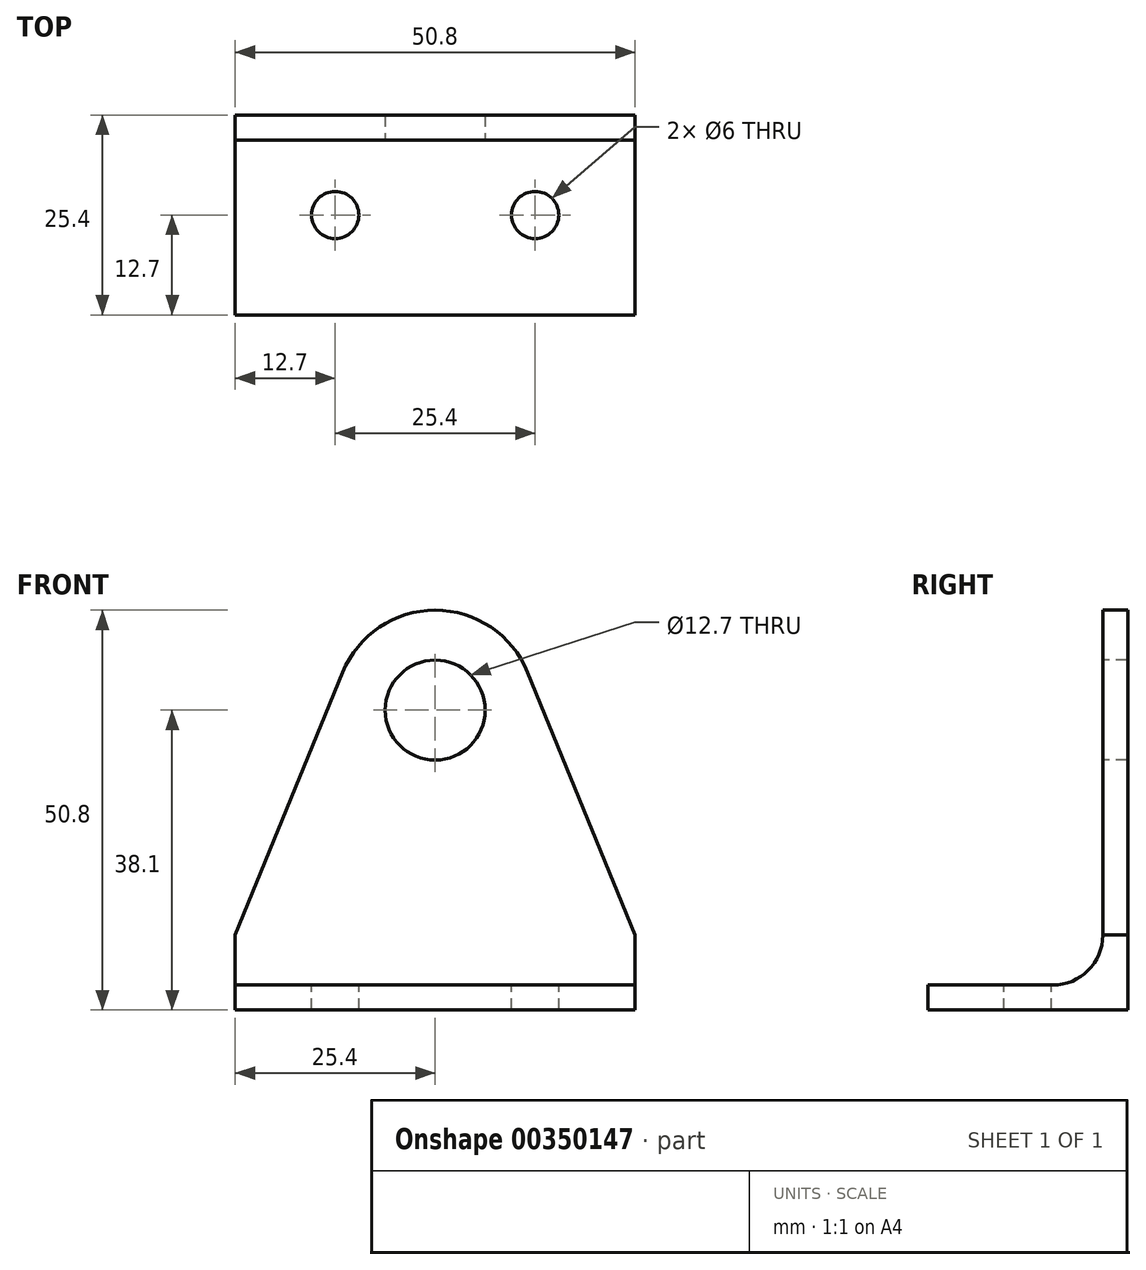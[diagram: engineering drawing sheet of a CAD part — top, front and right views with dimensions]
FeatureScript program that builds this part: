
annotation { "Feature Type Name" : "Feature", "Feature Type Description" : "" }
export const myFeature = defineFeature(function(context is Context, id is Id, definition is map)
    precondition{}
    {
        {
            var Q0;
            Q0=qCreatedBy(makeId("Right.planeOp"),FACE);
            var sketch = newSketch(context, id + "F0", { "sketchPlane" : qUnion([Q0])});
            skLineSegment(sketch, "E0", {"start": v(0, 0) * mm, "end": v(25.4, 0) * mm});
            skLineSegment(sketch, "E1", {"start": v(25.4, 0) * mm, "end": v(25.4, 50.8) * mm});
            skLineSegment(sketch, "E2.0", {"start": v(22.23, 3.17) * mm, "end": v(22.23, 50.8) * mm});
            skLineSegment(sketch, "E2.1", {"start": v(0, 3.17) * mm, "end": v(22.23, 3.17) * mm});
            skLineSegment(sketch, "E3", {"start": v(22.23, 50.8) * mm, "end": v(25.4, 50.8) * mm});
            skLineSegment(sketch, "E4", {"start": v(0, 3.17) * mm, "end": v(0, 0) * mm});
            skSolve(sketch);
        }
        {
            var Q0;
            Q0=makeQuery(id+"F0.imprint","IMPRINT",FACE,{"disambiguationData":[TD([[makeQuery(id+"F0.imprint","IMPRINT",EDGE,{"derivedFrom":sQuery(id+"F0.wireOp",EDGE,"E0")}),1.0]])]});
            extrude(context, id + "F1", {"entities" : qUnion([Q0]), "endBound" : BoundingType.SYMMETRIC, "depth" : 50.8 * mm});
        }
        {
            var Q0;
            Q0=makeQuery(id+"F1.opExtrude","SWEPT_EDGE",EDGE,{"disambiguationData":[OSD([sQuery(id+"F0.wireOp",EDGE,"E2.0"),sQuery(id+"F0.wireOp",EDGE,"E2.1")])]});
            fillet(context, id + "F2", {"entities" : qUnion([Q0]), "radius" : 6.35 * mm, "tangentPropagation" : true, "allowEdgeOverflow" : false});
        }
        {
            var Q0;
            Q0=makeQuery(id+"F1.opExtrude","SWEPT_FACE",FACE,{"disambiguationData":[OSD([sQuery(id+"F0.wireOp",EDGE,"E2.1")])]});
            var sketch = newSketch(context, id + "F3", { "sketchPlane" : qUnion([Q0])});
            skPoint(sketch, "E5.positionSnap0", {"position": v(-25.4, 7.94) * mm});
            skPoint(sketch, "E6", {"position": v(-12.7, 12.7) * mm});
            skPoint(sketch, "E7", {"position": v(12.7, 12.7) * mm});
            skSolve(sketch);
        }
        {
            var Q0;
            Q0=sQuery(id+"F3.wireOp",VERTEX,"E6");
            var Q1;
            Q1=sQuery(id+"F3.wireOp",VERTEX,"E7");
            var Q2;
            Q2=makeQuery(id+"F1.opExtrude","SWEPT_BODY",BODY,{"disambiguationData":[OSD([sQuery(id+"F0.wireOp",EDGE,"E0"),sQuery(id+"F0.wireOp",EDGE,"E1"),sQuery(id+"F0.wireOp",EDGE,"E2.0"),sQuery(id+"F0.wireOp",EDGE,"E2.1"),sQuery(id+"F0.wireOp",EDGE,"E3"),sQuery(id+"F0.wireOp",EDGE,"E4")])]});
            hole(context, id + "F4", {"style" : HoleStyle.SIMPLE, "endStyle" : HoleEndStyle.THROUGH, "holeDiameter" : 6 * mm, "isTappedThrough" : true, "tappedDepth" : 12 * mm, "tapClearance" : 3, "locations" : qUnion([Q0, Q1]), "scope" : qUnion([Q2])});
        }
        {
            var Q0;
            Q0=makeQuery(id+"F1.opExtrude","SWEPT_FACE",FACE,{"disambiguationData":[OSD([sQuery(id+"F0.wireOp",EDGE,"E2.0")])]});
            var sketch = newSketch(context, id + "F5", { "sketchPlane" : qUnion([Q0])});
            skPoint(sketch, "E8.centerSnap0", {"position": v(0, 9.52) * mm});
            skCircle(sketch, "E9", {"center": v(0, 38.1) * mm, "radius": 12.7 * mm});
            skCircle(sketch, "E10", {"center": v(0, 38.1) * mm, "radius": 6.35 * mm});
            skLineSegment(sketch, "E11", {"start": v(-25.4, 9.52) * mm, "end": v(-11.76, 42.9) * mm});
            skLineSegment(sketch, "E12", {"start": v(25.4, 9.52) * mm, "end": v(11.76, 42.9) * mm});
            skSolve(sketch);
        }
        {
            var Q0;
            {var subQ0=sQuery(id+"F5.wireOp",EDGE,"E11");Q0=makeQuery(id+"F5.imprint","IMPRINT",FACE,{"disambiguationData":[TD([[makeQuery(id+"F5.imprint","IMPRINT",EDGE,{"derivedFrom":subQ0}),1.0]])]});}
            var Q1;
            {var subQ0=sQuery(id+"F5.wireOp",EDGE,"E12");Q1=makeQuery(id+"F5.imprint","IMPRINT",FACE,{"disambiguationData":[TD([[makeQuery(id+"F5.imprint","IMPRINT",EDGE,{"derivedFrom":subQ0}),-1.0]])]});}
            var Q2;
            Q2=makeQuery(id+"F5.imprint","IMPRINT",FACE,{"disambiguationData":[TD([[makeQuery(id+"F5.imprint","IMPRINT",EDGE,{"derivedFrom":sQuery(id+"F5.wireOp",EDGE,"E10")}),1.0]])]});
            extrude(context, id + "F6", {"entities" : qUnion([Q0, Q1, Q2]), "operationType" : NewBodyOperationType.REMOVE, "endBound" : BoundingType.THROUGH_ALL, "oppositeDirection" : true, "depth" : 25 * mm});
        }
    });
